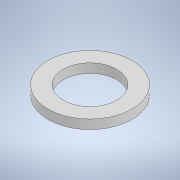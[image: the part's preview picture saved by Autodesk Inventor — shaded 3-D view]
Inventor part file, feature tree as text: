
AUTODESK INVENTOR PART (.ipt)
format: ipt  version: 2021 (Build 250183000, 183)  size: 99,328 bytes
history: native  units: mm
features: extrude x1, sketch x1
ambient origin geometry x8: Origin, YZ Plane, XZ Plane, XY Plane, X Axis, Y Axis, Z Axis, Center Point
bodies: Solid1 (feature_tree)
feature tree (2):
  extrude  "Extrusion1"  Depth=1.5mm
  sketch  "Sketch1"  dims[d0=8.8mm d1=13.8mm d2=1.5mm d3=0.0mm]
